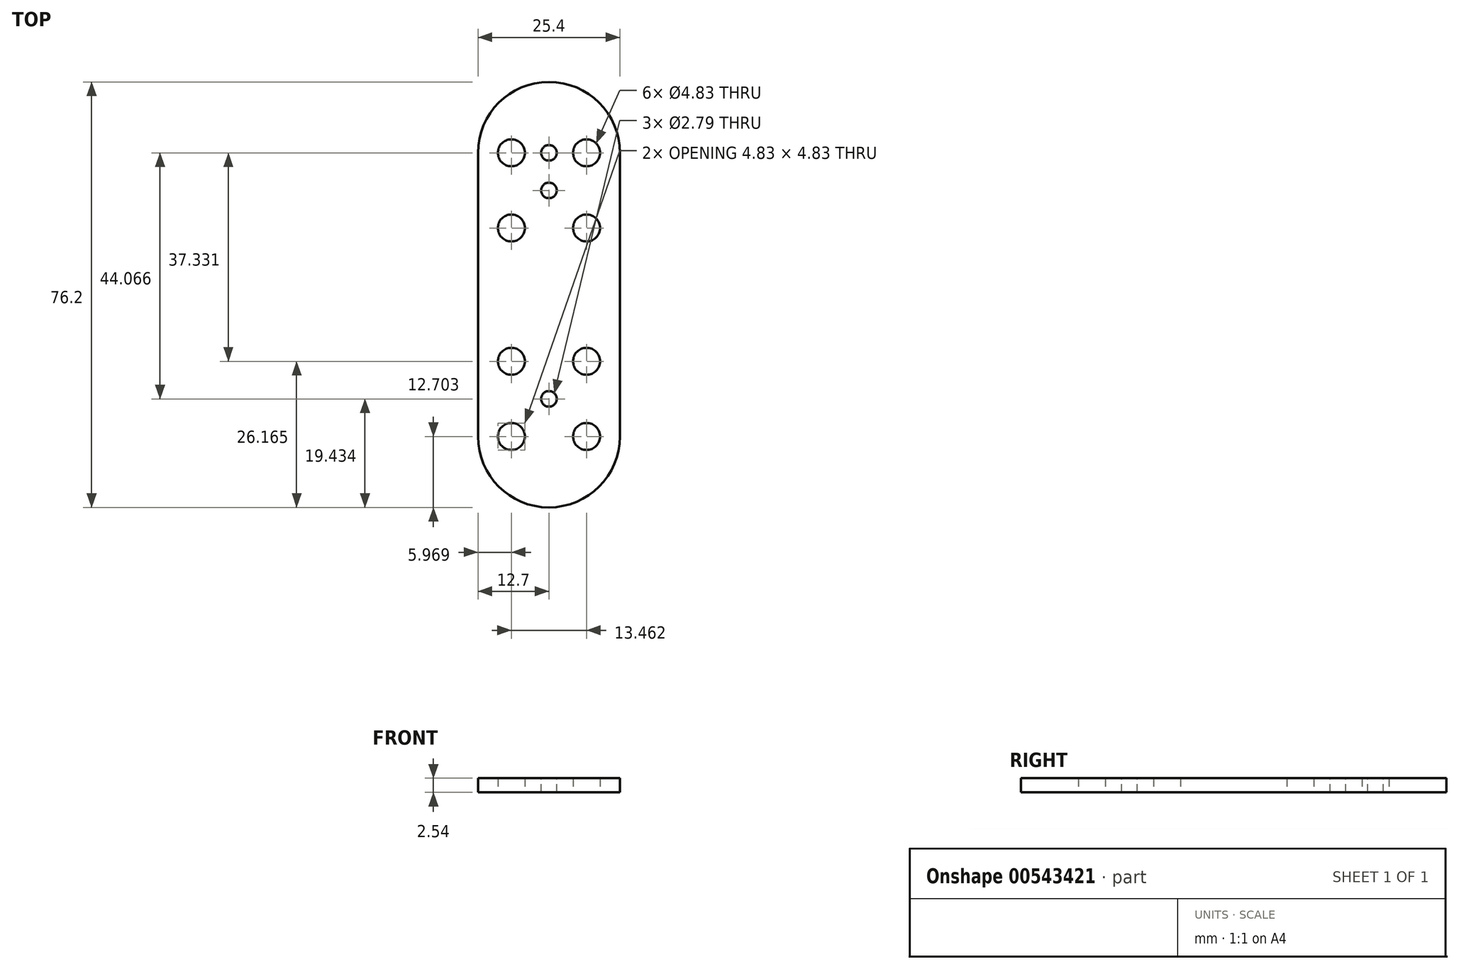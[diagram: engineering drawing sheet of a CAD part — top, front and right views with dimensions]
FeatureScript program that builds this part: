
annotation { "Feature Type Name" : "Feature", "Feature Type Description" : "" }
export const myFeature = defineFeature(function(context is Context, id is Id, definition is map)
    precondition{}
    {
        {
            var Q0;
            Q0=qCreatedBy(makeId("Top.planeOp"),FACE);
            var sketch = newSketch(context, id + "F0", { "sketchPlane" : qUnion([Q0])});
            skLineSegment(sketch, "E0.left", {"start": v(12.7, 0) * mm, "end": v(12.7, -50.8) * mm});
            skLineSegment(sketch, "E0.right", {"start": v(-12.7, 0) * mm, "end": v(-12.7, -50.8) * mm});
            skPoint(sketch, "E0.middle", {"position": v(0, 0) * mm});
            skLineSegment(sketch, "E1.bottom", {"start": v(6.73, -50.8) * mm, "end": v(-6.73, -50.8) * mm});
            skLineSegment(sketch, "E1.top", {"start": v(6.73, -37.33) * mm, "end": v(-6.73, -37.33) * mm});
            skLineSegment(sketch, "E1.left", {"start": v(6.73, -50.8) * mm, "end": v(6.73, -37.33) * mm});
            skLineSegment(sketch, "E1.right", {"start": v(-6.73, -50.8) * mm, "end": v(-6.73, -37.33) * mm});
            skPoint(sketch, "E1.middle", {"position": v(0, -44.07) * mm});
            skCircle(sketch, "E2", {"center": v(-6.73, -37.33) * mm, "radius": 2.41 * mm});
            skCircle(sketch, "E3", {"center": v(6.73, -37.33) * mm, "radius": 2.41 * mm});
            skCircle(sketch, "E4", {"center": v(6.73, -50.8) * mm, "radius": 2.41 * mm});
            skCircle(sketch, "E5", {"center": v(-6.73, -50.8) * mm, "radius": 2.41 * mm});
            skLineSegment(sketch, "E6", {"start": v(-12.7, -50.8) * mm, "end": v(-4.32, -50.8) * mm});
            skLineSegment(sketch, "E7", {"start": v(-12.7, 0) * mm, "end": v(12.7, 0) * mm});
            skPoint(sketch, "E8.orphan", {"position": v(-12.7, 50.8) * mm});
            skPoint(sketch, "E9.orphan", {"position": v(12.7, 50.8) * mm});
            skLineSegment(sketch, "E10", {"start": v(-12.7, -25.4) * mm, "end": v(12.7, -25.4) * mm});
            skCircle(sketch, "E11.MirrorC", {"center": v(-6.73, -13.47) * mm, "radius": 2.41 * mm});
            skCircle(sketch, "E12.MirrorC", {"center": v(-6.73, 0) * mm, "radius": 2.41 * mm});
            skCircle(sketch, "E13.MirrorC", {"center": v(6.73, -13.47) * mm, "radius": 2.41 * mm});
            skCircle(sketch, "E14.MirrorC", {"center": v(6.73, 0) * mm, "radius": 2.41 * mm});
            skArc(sketch, "E15", {"start": v(12.7, 0) * mm, "mid": v(0, 12.7) * mm, "end": v(-12.7, 0) * mm});
            skArc(sketch, "E16", {"start": v(-12.7, -50.8) * mm, "mid": v(0, -63.5) * mm, "end": v(12.7, -50.8) * mm});
            skLineSegment(sketch, "E17.trimOffspring", {"start": v(4.32, -50.8) * mm, "end": v(12.7, -50.8) * mm});
            skSolve(sketch);
        }
        {
            var Q0;
            Q0=qSketchRegion(id+"F0",true);
            var Q1;
            {var subQ5=sQuery(id+"F0.wireOp",EDGE,"E4");var subQ10=sQuery(id+"F0.wireOp",EDGE,"E1.bottom");var subQ15=makeQuery(id+"F0.imprint","INTERSECT",VERTEX,{"derivedFrom":[subQ10,subQ5]});Q1=makeQuery(id+"F0.imprint","IMPRINT",FACE,{"disambiguationData":[TD([[makeQuery(id+"F0.imprint","IMPRINT",EDGE,{"disambiguationData":[TD([[subQ15,-1.0]])],"derivedFrom":subQ10}),-1.0]])]});}
            extrude(context, id + "F1", {"entities" : qUnion([Q0, Q1]), "depth" : 2.54 * mm, "offsetDistance" : 25.4 * mm});
        }
        {
            var Q0;
            Q0=makeQuery(id+"F1.opExtrude","CAP_FACE",FACE,{"disambiguationData":[OSD([sQuery(id+"F0.wireOp",EDGE,"E0.left"),sQuery(id+"F0.wireOp",EDGE,"E0.right"),sQuery(id+"F0.wireOp",EDGE,"E2"),sQuery(id+"F0.wireOp",EDGE,"E3"),sQuery(id+"F0.wireOp",EDGE,"E4"),sQuery(id+"F0.wireOp",EDGE,"E5"),sQuery(id+"F0.wireOp",EDGE,"PWbGE1YV-YYys-uQrc-CrKx-6ADu0uZc2XtY"),sQuery(id+"F0.wireOp",EDGE,"t0C233Ww-Tjgr-lEmG-p7Nm-2mTDBtev8aHC")])],"isStart":false});
            var sketch = newSketch(context, id + "F2", { "sketchPlane" : qUnion([Q0])});
            skCircle(sketch, "E18", {"center": v(0, 0) * mm, "radius": 1.4 * mm});
            skLineSegment(sketch, "E19", {"start": v(-6.73, 0) * mm, "end": v(6.73, -13.47) * mm});
            skLineSegment(sketch, "E20", {"start": v(6.73, 0) * mm, "end": v(-6.73, -13.47) * mm});
            skCircle(sketch, "E21", {"center": v(0, -6.73) * mm, "radius": 1.4 * mm});
            skCircle(sketch, "E22.MirrorC", {"center": v(0, -44.07) * mm, "radius": 1.4 * mm});
            skSolve(sketch);
        }
        {
            var Q0;
            Q0=qSketchRegion(id+"F2",true);
            extrude(context, id + "F3", {"entities" : qUnion([Q0]), "operationType" : NewBodyOperationType.REMOVE, "endBound" : BoundingType.THROUGH_ALL, "oppositeDirection" : true, "depth" : 6.35 * mm, "offsetDistance" : 25.4 * mm});
        }
    });
